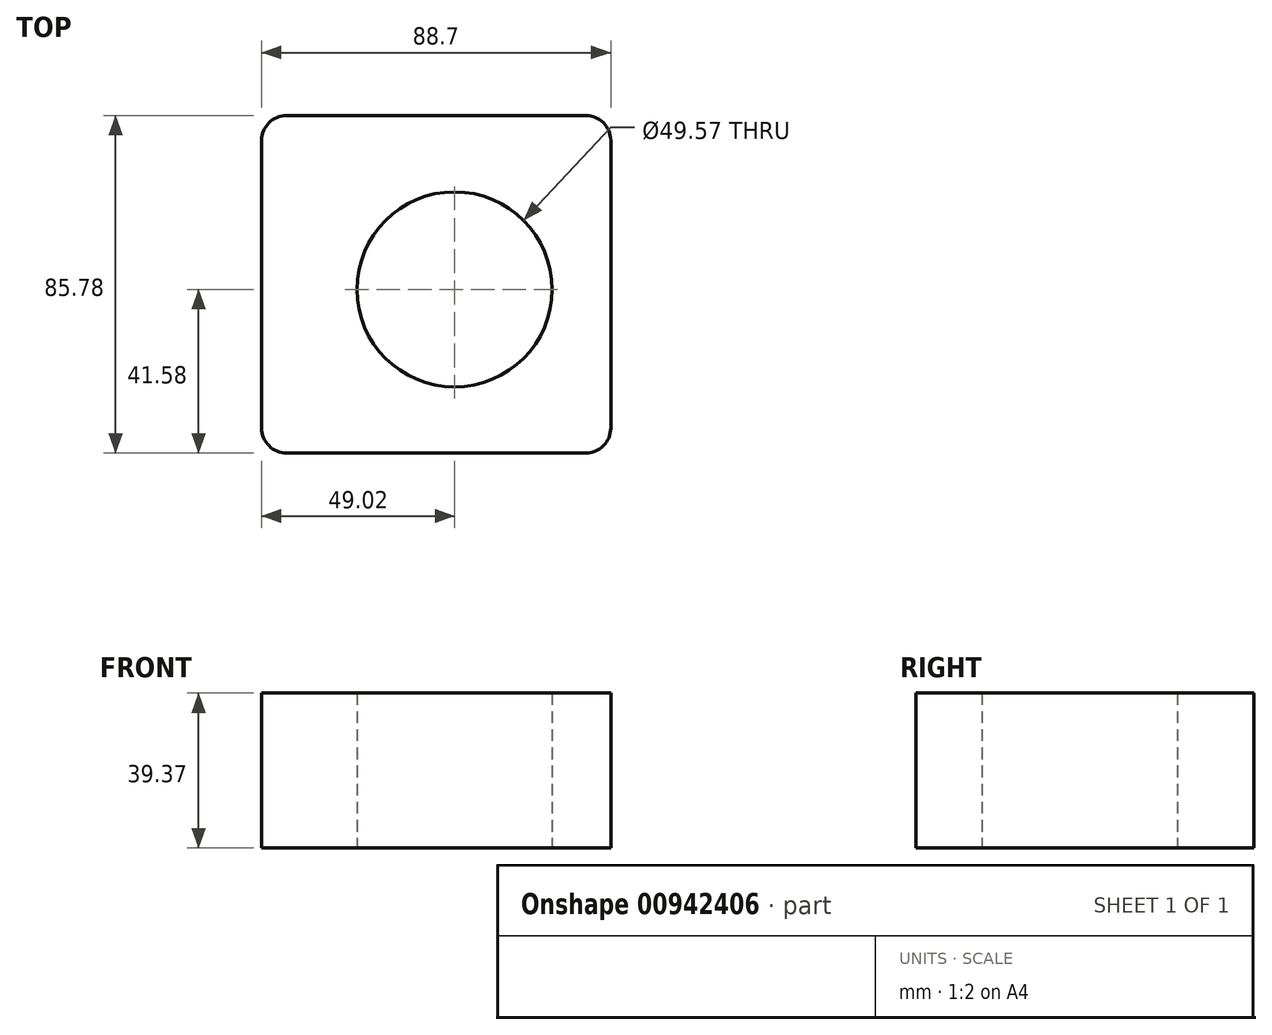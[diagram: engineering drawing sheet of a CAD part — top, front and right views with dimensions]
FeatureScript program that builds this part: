
annotation { "Feature Type Name" : "Feature", "Feature Type Description" : "" }
export const myFeature = defineFeature(function(context is Context, id is Id, definition is map)
    precondition{}
    {
        {
            var Q0;
            Q0=qCreatedBy(makeId("Top.planeOp"),FACE);
            var sketch = newSketch(context, id + "F0", { "sketchPlane" : qUnion([Q0])});
            skLineSegment(sketch, "E0.bottom", {"start": v(-42.67, 44.2) * mm, "end": v(33.33, 44.2) * mm});
            skLineSegment(sketch, "E0.top", {"start": v(-42.67, -41.58) * mm, "end": v(33.33, -41.58) * mm});
            skLineSegment(sketch, "E0.left", {"start": v(-49.02, 37.85) * mm, "end": v(-49.02, -35.23) * mm});
            skLineSegment(sketch, "E0.right", {"start": v(39.68, 37.85) * mm, "end": v(39.68, -35.23) * mm});
            skPoint(sketch, "E1.visualSharp", {"position": v(-49.02, 44.2) * mm});
            skArc(sketch, "E1.filletArc", {"start": v(-42.67, 44.2) * mm, "mid": v(-47.16, 42.34) * mm, "end": v(-49.02, 37.85) * mm});
            skPoint(sketch, "E2.visualSharp", {"position": v(39.68, 44.2) * mm});
            skArc(sketch, "E2.filletArc", {"start": v(39.68, 37.85) * mm, "mid": v(37.82, 42.34) * mm, "end": v(33.33, 44.2) * mm});
            skPoint(sketch, "E3.visualSharp", {"position": v(-49.02, -41.58) * mm});
            skArc(sketch, "E3.filletArc", {"start": v(-49.02, -35.23) * mm, "mid": v(-47.16, -39.72) * mm, "end": v(-42.67, -41.58) * mm});
            skPoint(sketch, "E4.visualSharp", {"position": v(39.68, -41.58) * mm});
            skArc(sketch, "E4.filletArc", {"start": v(33.33, -41.58) * mm, "mid": v(37.82, -39.72) * mm, "end": v(39.68, -35.23) * mm});
            skCircle(sketch, "E5", {"center": v(0, 0) * mm, "radius": 24.78 * mm});
            skSolve(sketch);
        }
        {
            var Q0;
            Q0=makeQuery(id+"F0.imprint","IMPRINT",FACE,{"disambiguationData":[TD([[makeQuery(id+"F0.imprint","IMPRINT",EDGE,{"derivedFrom":sQuery(id+"F0.wireOp",EDGE,"E0.bottom")}),-1.0]])]});
            extrude(context, id + "F1", {"entities" : qUnion([Q0]), "depth" : 39.37 * mm, "offsetDistance" : 25.4 * mm});
        }
    });
